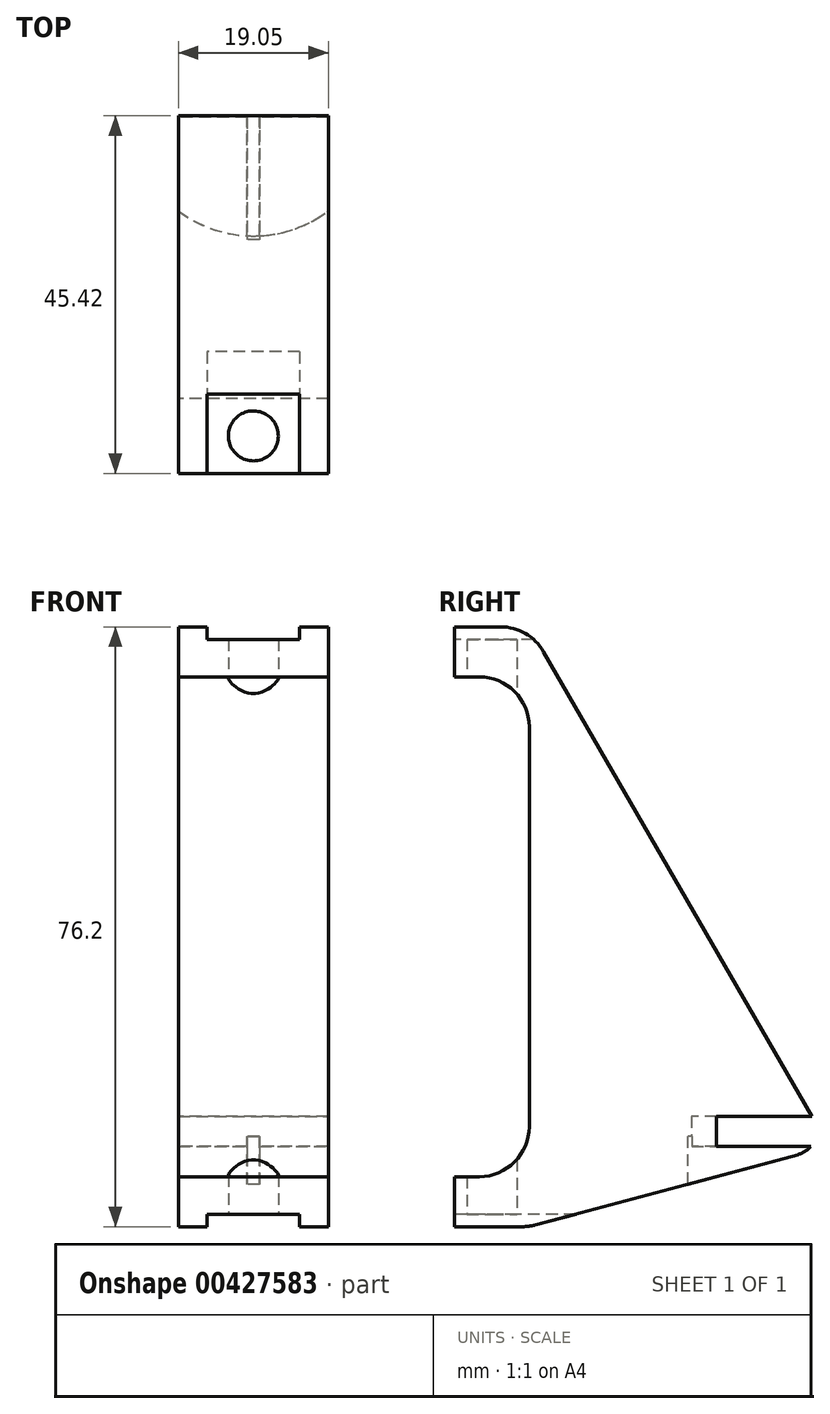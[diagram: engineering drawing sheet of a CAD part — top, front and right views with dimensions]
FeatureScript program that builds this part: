
annotation { "Feature Type Name" : "Feature", "Feature Type Description" : "" }
export const myFeature = defineFeature(function(context is Context, id is Id, definition is map)
    precondition{}
    {
        {
            var Q0;
            Q0=qCreatedBy(makeId("Right.planeOp"),FACE);
            var sketch = newSketch(context, id + "F0", { "sketchPlane" : qUnion([Q0])});
            skLineSegment(sketch, "E0", {"start": v(-2.07, 3.58) * mm, "end": v(-36.27, 62.82) * mm});
            skLineSegment(sketch, "E1", {"start": v(-37.3, -10) * mm, "end": v(-4, -1.07) * mm});
            skPoint(sketch, "E2.visualSharp", {"position": v(-38.1, 66) * mm});
            skPoint(sketch, "E3.visualSharp", {"position": v(0, 0) * mm});
            skArc(sketch, "E3.filletArc", {"start": v(-4, -1.07) * mm, "mid": v(-1.89, 0.78) * mm, "end": v(-2.07, 3.58) * mm});
            skPoint(sketch, "E4.visualSharp", {"position": v(-38.1, -10.2) * mm});
            skLineSegment(sketch, "E5", {"start": v(-41.77, 66) * mm, "end": v(-47.63, 66) * mm});
            skLineSegment(sketch, "E6", {"start": v(-47.63, 66) * mm, "end": v(-47.63, 59.64) * mm});
            skLineSegment(sketch, "E7", {"start": v(-47.63, 59.64) * mm, "end": v(-44.45, 59.64) * mm});
            skLineSegment(sketch, "E8", {"start": v(-38.94, -10.2) * mm, "end": v(-47.62, -10.2) * mm});
            skLineSegment(sketch, "E9", {"start": v(-47.62, -10.2) * mm, "end": v(-47.62, -3.86) * mm});
            skLineSegment(sketch, "E10", {"start": v(-47.62, -3.86) * mm, "end": v(-44.45, -3.86) * mm});
            skLineSegment(sketch, "E11", {"start": v(-38.1, 2.5) * mm, "end": v(-38.1, 53.3) * mm});
            skPoint(sketch, "E12.visualSharp", {"position": v(-38.1, 59.64) * mm});
            skArc(sketch, "E12.filletArc", {"start": v(-38.1, 53.3) * mm, "mid": v(-39.96, 57.78) * mm, "end": v(-44.45, 59.64) * mm});
            skPoint(sketch, "E13.visualSharp", {"position": v(-38.1, -3.86) * mm});
            skArc(sketch, "E13.filletArc", {"start": v(-44.45, -3.86) * mm, "mid": v(-39.96, -2) * mm, "end": v(-38.1, 2.5) * mm});
            skArc(sketch, "E14.filletArc", {"start": v(-38.94, -10.2) * mm, "mid": v(-38.1, -10.15) * mm, "end": v(-37.3, -10) * mm});
            skArc(sketch, "E15.filletArc", {"start": v(-36.27, 62.82) * mm, "mid": v(-38.6, 65.14) * mm, "end": v(-41.77, 66) * mm});
            skSolve(sketch);
        }
        {
            var Q0;
            Q0 = qSketchRegion(id + "F0", true);
            extrude(context, id + "F1", {"entities" : qUnion([Q0]), "depth" : 19.05 * mm});
        }
        {
            var Q0;
            Q0=makeQuery(id+"F1.opExtrude","SWEPT_FACE",FACE,{"disambiguationData":[OSD([sQuery(id+"F0.wireOp",EDGE,"E8")])]});
            var sketch = newSketch(context, id + "F2", { "sketchPlane" : qUnion([Q0])});
            skLineSegment(sketch, "E16", {"start": v(9.53, 47.62) * mm, "end": v(9.53, 38.1) * mm, "construction": true});
            skPoint(sketch, "E17", {"position": v(9.53, 42.86) * mm});
            skSolve(sketch);
        }
        {
            var Q0;
            Q0=sQuery(id+"F2.wireOp",VERTEX,"E17");
            var Q1;
            Q1=makeQuery(id+"F1.opExtrude","SWEPT_BODY",BODY,{"disambiguationData":[OSD([sQuery(id+"F0.wireOp",EDGE,"E0"),sQuery(id+"F0.wireOp",EDGE,"E1"),sQuery(id+"F0.wireOp",EDGE,"E3.filletArc"),sQuery(id+"F0.wireOp",EDGE,"E5"),sQuery(id+"F0.wireOp",EDGE,"E6"),sQuery(id+"F0.wireOp",EDGE,"E7"),sQuery(id+"F0.wireOp",EDGE,"E8"),sQuery(id+"F0.wireOp",EDGE,"E9"),sQuery(id+"F0.wireOp",EDGE,"E10"),sQuery(id+"F0.wireOp",EDGE,"E11"),sQuery(id+"F0.wireOp",EDGE,"E12.filletArc"),sQuery(id+"F0.wireOp",EDGE,"E13.filletArc"),sQuery(id+"F0.wireOp",EDGE,"E14.filletArc"),sQuery(id+"F0.wireOp",EDGE,"E15.filletArc")])]});
            hole(context, id + "F3", {"style" : HoleStyle.SIMPLE, "endStyle" : HoleEndStyle.THROUGH, "holeDiameter" : 6.35 * mm, "isTappedThrough" : true, "tappedDepth" : 12.7 * mm, "tapClearance" : 3, "locations" : qUnion([Q0]), "scope" : qUnion([Q1])});
        }
        {
            var Q0;
            Q0=qCreatedBy(makeId("Top.planeOp"),FACE);
            var sketch = newSketch(context, id + "F4", { "sketchPlane" : qUnion([Q0])});
            skLineSegment(sketch, "E18.bottom", {"start": v(10.32, 17.94) * mm, "end": v(8.73, 17.94) * mm});
            skLineSegment(sketch, "E18.top", {"start": v(10.32, -17.94) * mm, "end": v(8.73, -17.94) * mm});
            skLineSegment(sketch, "E18.left", {"start": v(10.32, 17.94) * mm, "end": v(10.32, -17.94) * mm});
            skLineSegment(sketch, "E18.right", {"start": v(8.73, 17.94) * mm, "end": v(8.73, -17.94) * mm});
            skPoint(sketch, "E18.middle", {"position": v(9.53, 0) * mm});
            skSolve(sketch);
        }
        {
            var Q0;
            Q0 = qSketchRegion(id + "F4", true);
            extrude(context, id + "F5", {"entities" : qUnion([Q0]), "operationType" : NewBodyOperationType.REMOVE, "oppositeDirection" : true, "depth" : 25.4 * mm, "hasSecondDirection" : true, "secondDirectionOppositeDirection" : false, "secondDirectionDepth" : 1.27 * mm});
        }
        {
            var Q0;
            Q0=qCreatedBy(makeId("Top.planeOp"),FACE);
            var sketch = newSketch(context, id + "F6", { "sketchPlane" : qUnion([Q0])});
            skCircle(sketch, "E19", {"center": v(9.53, -1.59) * mm, "radius": 15.88 * mm});
            skSolve(sketch);
        }
        {
            var Q0;
            Q0=makeQuery(id+"F6.imprint","IMPRINT",FACE,{"disambiguationData":[TD([[makeQuery(id+"F6.imprint","IMPRINT",EDGE,{"derivedFrom":sQuery(id+"F6.wireOp",EDGE,"E19")}),1.0]])]});
            extrude(context, id + "F7", {"entities" : qUnion([Q0]), "operationType" : NewBodyOperationType.REMOVE, "depth" : 3.8 * mm});
        }
        {
            var Q0;
            Q0=makeQuery(id+"F1.opExtrude","SWEPT_FACE",FACE,{"disambiguationData":[OSD([sQuery(id+"F0.wireOp",EDGE,"E6")])]});
            var sketch = newSketch(context, id + "F8", { "sketchPlane" : qUnion([Q0])});
            skLineSegment(sketch, "E20.bottom", {"start": v(15.4, 64.4) * mm, "end": v(3.65, 64.4) * mm});
            skLineSegment(sketch, "E20.top", {"start": v(15.4, 67.58) * mm, "end": v(3.65, 67.58) * mm});
            skLineSegment(sketch, "E20.left", {"start": v(15.4, 64.4) * mm, "end": v(15.4, 67.58) * mm});
            skLineSegment(sketch, "E20.right", {"start": v(3.65, 64.4) * mm, "end": v(3.65, 67.58) * mm});
            skPoint(sketch, "E20.middle", {"position": v(9.53, 66) * mm});
            skSolve(sketch);
        }
        {
            var Q0;
            Q0 = qSketchRegion(id + "F8", true);
            extrude(context, id + "F9", {"entities" : qUnion([Q0]), "operationType" : NewBodyOperationType.REMOVE, "oppositeDirection" : true, "depth" : 25.4 * mm});
        }
        {
            var Q0;
            Q0=makeQuery(id+"F1.opExtrude","SWEPT_FACE",FACE,{"disambiguationData":[OSD([sQuery(id+"F0.wireOp",EDGE,"E9")])]});
            var sketch = newSketch(context, id + "F10", { "sketchPlane" : qUnion([Q0])});
            skLineSegment(sketch, "E21.bottom", {"start": v(15.4, -8.62) * mm, "end": v(3.65, -8.62) * mm});
            skLineSegment(sketch, "E21.top", {"start": v(15.4, -11.8) * mm, "end": v(3.65, -11.8) * mm});
            skLineSegment(sketch, "E21.left", {"start": v(15.4, -8.62) * mm, "end": v(15.4, -11.8) * mm});
            skLineSegment(sketch, "E21.right", {"start": v(3.65, -8.62) * mm, "end": v(3.65, -11.8) * mm});
            skPoint(sketch, "E21.middle", {"position": v(9.53, -10.2) * mm});
            skSolve(sketch);
        }
        {
            var Q0;
            Q0 = qSketchRegion(id + "F10", true);
            extrude(context, id + "F11", {"entities" : qUnion([Q0]), "operationType" : NewBodyOperationType.REMOVE, "oppositeDirection" : true, "depth" : 25.4 * mm});
        }
    });
